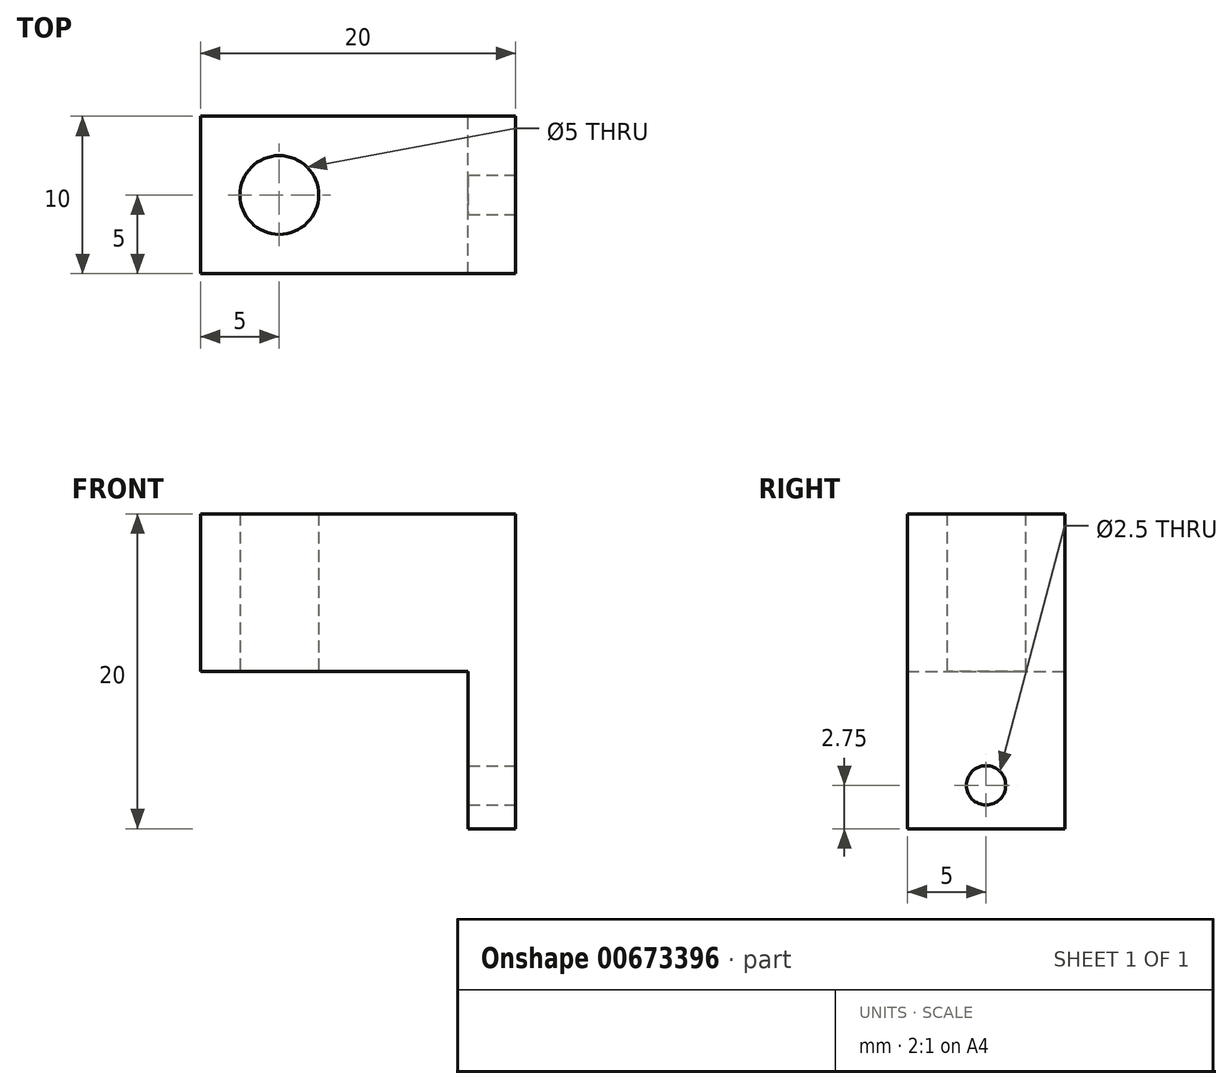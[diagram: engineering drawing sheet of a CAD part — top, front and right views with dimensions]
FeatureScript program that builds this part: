
annotation { "Feature Type Name" : "Feature", "Feature Type Description" : "" }
export const myFeature = defineFeature(function(context is Context, id is Id, definition is map)
    precondition{}
    {
        {
            var Q0;
            Q0=qCreatedBy(makeId("Top.planeOp"),FACE);
            var sketch = newSketch(context, id + "F0", { "sketchPlane" : qUnion([Q0])});
            skLineSegment(sketch, "E0.bottom", {"start": v(0, 0) * mm, "end": v(20, 0) * mm});
            skLineSegment(sketch, "E0.top", {"start": v(0, -10) * mm, "end": v(20, -10) * mm});
            skLineSegment(sketch, "E0.left", {"start": v(0, 0) * mm, "end": v(0, -10) * mm});
            skLineSegment(sketch, "E0.right", {"start": v(20, 0) * mm, "end": v(20, -10) * mm});
            skCircle(sketch, "E1", {"center": v(5, -5) * mm, "radius": 2.5 * mm});
            skPoint(sketch, "E1.centerSnap0", {"position": v(0, -5) * mm});
            skSolve(sketch);
        }
        {
            var Q0;
            Q0=makeQuery(id+"F0.imprint","IMPRINT",FACE,{"disambiguationData":[TD([[makeQuery(id+"F0.imprint","IMPRINT",EDGE,{"derivedFrom":sQuery(id+"F0.wireOp",EDGE,"E0.bottom")}),-1.0]])]});
            extrude(context, id + "F1", {"entities" : qUnion([Q0]), "depth" : 10 * mm, "offsetDistance" : 25 * mm});
        }
        {
            var Q0;
            Q0=makeQuery(id+"F1.opExtrude","CAP_FACE",FACE,{"disambiguationData":[OSD([sQuery(id+"F0.wireOp",EDGE,"E0.bottom"),sQuery(id+"F0.wireOp",EDGE,"E0.top"),sQuery(id+"F0.wireOp",EDGE,"E0.left"),sQuery(id+"F0.wireOp",EDGE,"E0.right"),sQuery(id+"F0.wireOp",EDGE,"E1")])],"isStart":true});
            var sketch = newSketch(context, id + "F2", { "sketchPlane" : qUnion([Q0])});
            skLineSegment(sketch, "E2.bottom", {"start": v(20, 10) * mm, "end": v(17, 10) * mm});
            skLineSegment(sketch, "E2.top", {"start": v(20, 0) * mm, "end": v(17, 0) * mm});
            skLineSegment(sketch, "E2.left", {"start": v(20, 10) * mm, "end": v(20, 0) * mm});
            skLineSegment(sketch, "E2.right", {"start": v(17, 10) * mm, "end": v(17, 0) * mm});
            skSolve(sketch);
        }
        {
            var Q0;
            Q0=makeQuery(id+"F2.imprint","IMPRINT",FACE,{"disambiguationData":[TD([[makeQuery(id+"F2.imprint","IMPRINT",EDGE,{"derivedFrom":sQuery(id+"F2.wireOp",EDGE,"E2.bottom")}),-1.0]])]});
            extrude(context, id + "F3", {"entities" : qUnion([Q0]), "operationType" : NewBodyOperationType.ADD, "depth" : 10 * mm, "offsetDistance" : 25 * mm});
        }
        {
            var Q0;
            Q0=makeQuery(id+"F3.boolean.opBoolean","MERGE",FACE,{"derivedFrom":[makeQuery(id+"F1.opExtrude","SWEPT_FACE",FACE,{"disambiguationData":[OSD([sQuery(id+"F0.wireOp",EDGE,"E0.right")])]}),makeQuery(id+"F3.opExtrude","SWEPT_FACE",FACE,{"disambiguationData":[OSD([sQuery(id+"F2.wireOp",EDGE,"E2.left")])]})]});
            var sketch = newSketch(context, id + "F4", { "sketchPlane" : qUnion([Q0])});
            skCircle(sketch, "E3", {"center": v(-5, -7.25) * mm, "radius": 1.25 * mm});
            skSolve(sketch);
        }
        {
            var Q0;
            Q0=makeQuery(id+"F4.imprint","IMPRINT",FACE,{"disambiguationData":[TD([[makeQuery(id+"F4.imprint","IMPRINT",EDGE,{"derivedFrom":sQuery(id+"F4.wireOp",EDGE,"E3")}),1.0]])]});
            extrude(context, id + "F5", {"entities" : qUnion([Q0]), "operationType" : NewBodyOperationType.REMOVE, "endBound" : BoundingType.UP_TO_NEXT, "oppositeDirection" : true, "depth" : 25 * mm, "offsetDistance" : 25 * mm});
        }
    });
